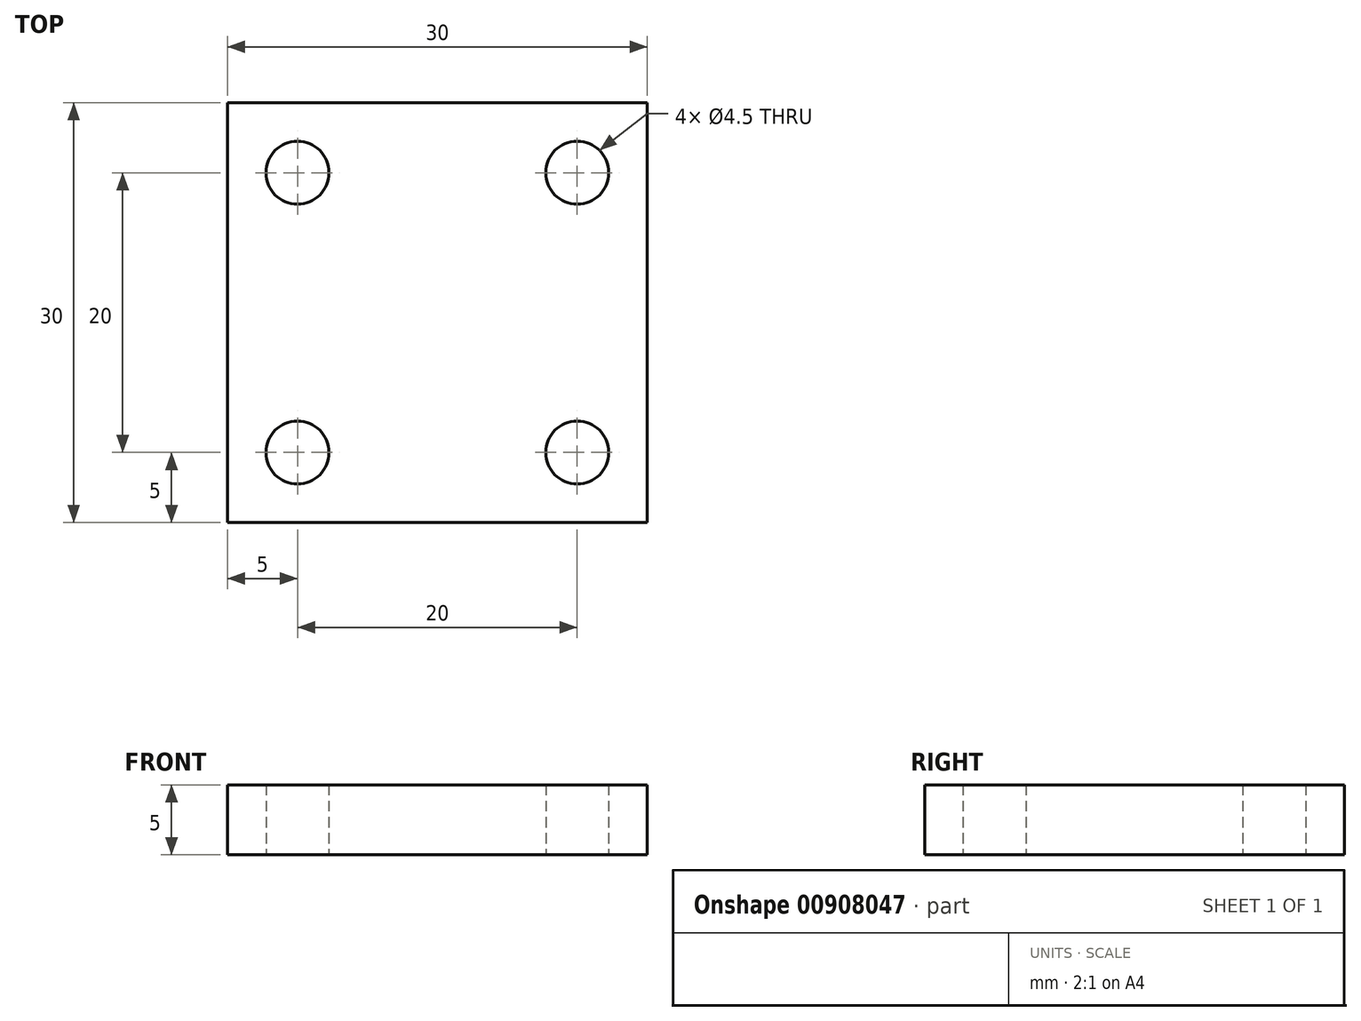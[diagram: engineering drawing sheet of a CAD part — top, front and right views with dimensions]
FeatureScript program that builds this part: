
annotation { "Feature Type Name" : "Feature", "Feature Type Description" : "" }
export const myFeature = defineFeature(function(context is Context, id is Id, definition is map)
    precondition{}
    {
        {
            var Q0;
            Q0=qCreatedBy(makeId("Top.planeOp"),FACE);
            var sketch = newSketch(context, id + "F0", { "sketchPlane" : qUnion([Q0])});
            skLineSegment(sketch, "E0.bottom", {"start": v(-15, 15) * mm, "end": v(15, 15) * mm});
            skLineSegment(sketch, "E0.top", {"start": v(-15, -15) * mm, "end": v(15, -15) * mm});
            skLineSegment(sketch, "E0.left", {"start": v(-15, 15) * mm, "end": v(-15, -15) * mm});
            skLineSegment(sketch, "E0.right", {"start": v(15, 15) * mm, "end": v(15, -15) * mm});
            skPoint(sketch, "E0.middle", {"position": v(0, 0) * mm});
            skCircle(sketch, "E1", {"center": v(-10, 10) * mm, "radius": 2.25 * mm});
            skCircle(sketch, "E2", {"center": v(-10, -10) * mm, "radius": 2.25 * mm});
            skCircle(sketch, "E3", {"center": v(10, -10) * mm, "radius": 2.25 * mm});
            skCircle(sketch, "E4", {"center": v(10, 10) * mm, "radius": 2.25 * mm});
            skSolve(sketch);
        }
        {
            var Q0;
            Q0=makeQuery(id+"F0.imprint","IMPRINT",FACE,{"disambiguationData":[TD([[makeQuery(id+"F0.imprint","IMPRINT",EDGE,{"derivedFrom":sQuery(id+"F0.wireOp",EDGE,"E0.bottom")}),-1.0]])]});
            extrude(context, id + "F1", {"entities" : qUnion([Q0]), "depth" : 5 * mm, "offsetDistance" : 25 * mm});
        }
    });
